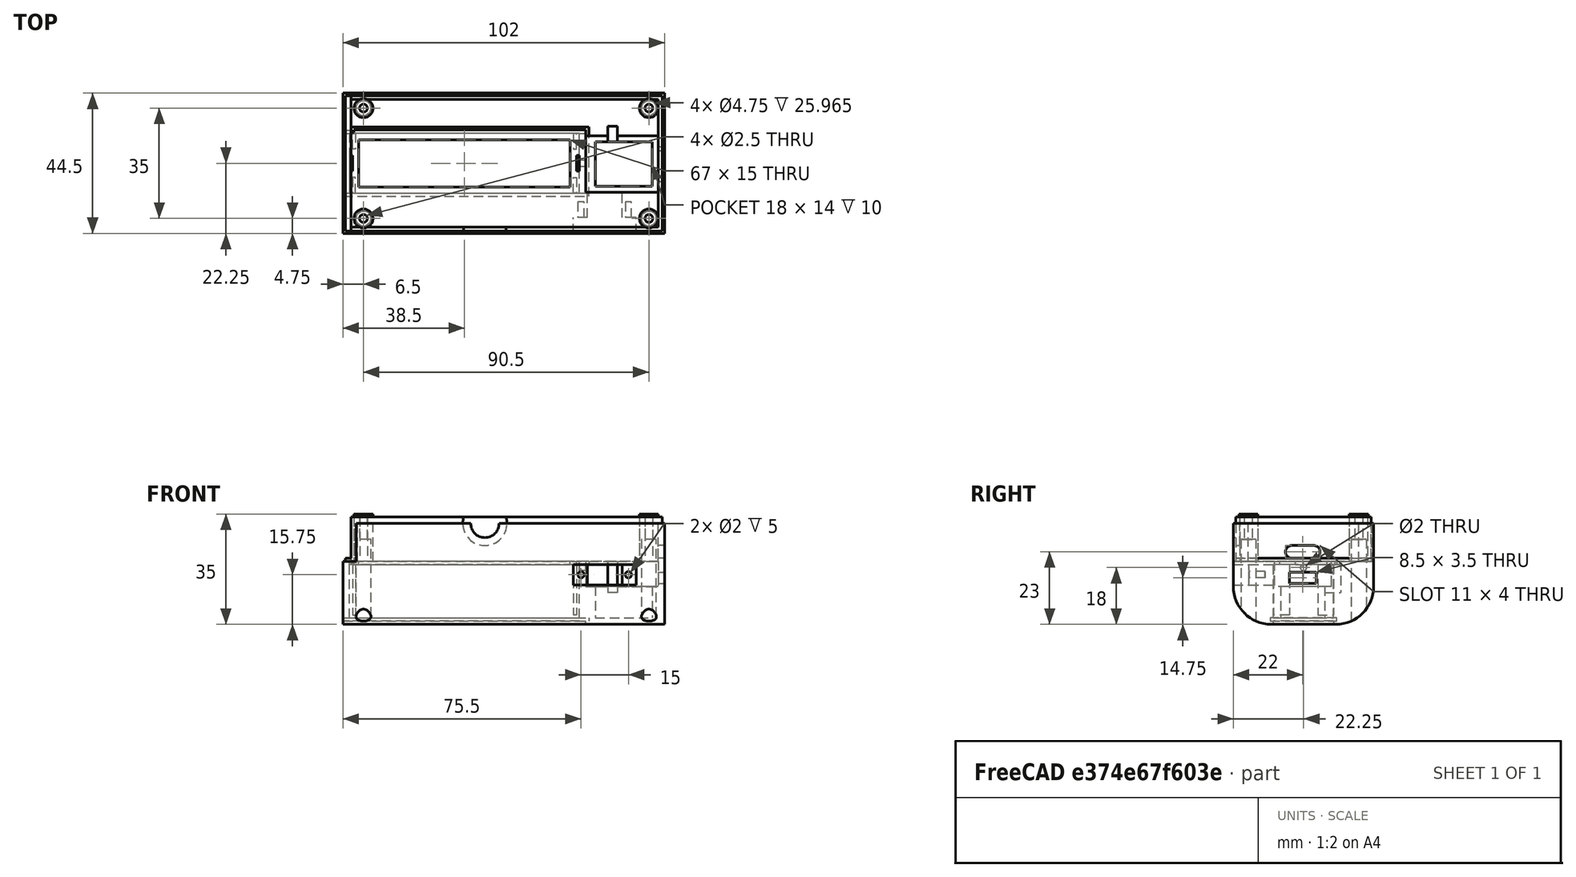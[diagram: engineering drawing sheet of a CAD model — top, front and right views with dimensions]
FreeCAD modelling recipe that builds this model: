
FCSTD DOCUMENT  (FreeCAD 0.20R)
Label: upper
License: All rights reserved
LicenseURL: http://en.wikipedia.org/wiki/All_rights_reserved
objects: Sketcher::SketchObject×27, PartDesign::Pocket×23, PartDesign::Pad×4, PartDesign::Plane×1, PartDesign::Fillet×1, PartDesign::Body×1
note: 85 computed .brp shape members not serialized (recipe doc carries the construction recipe); baked Part::Feature solids carry a one-line shape summary decoded from their .brp

FEATURE [Sketcher::SketchObject] Sketch  label="sketch_lower_base"
  FullyConstrained = true
  MapMode = 5
  Support = -> [XY_Plane]
  sketch-geometry (4):
    g0: LineSegment StartX=0 StartY=0 StartZ=0 EndX=102 EndY=0 EndZ=0
    g1: LineSegment StartX=102 StartY=0 StartZ=0 EndX=102 EndY=44.5 EndZ=0
    g2: LineSegment StartX=102 StartY=44.5 StartZ=0 EndX=0 EndY=44.5 EndZ=0
    g3: LineSegment StartX=0 StartY=44.5 StartZ=0 EndX=0 EndY=0 EndZ=0
  constraints (11):
    c: Coincident(g0,g1)
    c: Coincident(g1,g2)
    c: Coincident(g2,g3)
    c: Coincident(g3,g0)
    c: Horizontal(g0)
    c: Horizontal(g2)
    c: Vertical(g1)
    c: Vertical(g3)
    c: Coincident(g0,g-1)
    c: Distance(g2) = 102
    c: Distance(g3) = 44.5
FEATURE [PartDesign::Pad] Pad  label="pad_lower_base"
  Direction = (0,0,1)
  Length = 16
  Length2 = 10
  Profile = -> Sketch
  ReferenceAxis = -> Sketch [N_Axis]
  Type = 0
FEATURE [Sketcher::SketchObject] Sketch001  label="sketch_lower_base_hole"
  FullyConstrained = true
  MapMode = 5
  Placement = pos=(0,0,16) rot=(0,0,1;0rad)
  Support = -> [Pad]
  sketch-geometry (4):
    g0: LineSegment StartX=2.5 StartY=42.5 StartZ=0 EndX=100 EndY=42.5 EndZ=0
    g1: LineSegment StartX=100 StartY=42.5 StartZ=0 EndX=100 EndY=2 EndZ=0
    g2: LineSegment StartX=100 StartY=2 StartZ=0 EndX=2.5 EndY=2 EndZ=0
    g3: LineSegment StartX=2.5 StartY=2 StartZ=0 EndX=2.5 EndY=42.5 EndZ=0
  constraints (12):
    c: Coincident(g0,g1)
    c: Coincident(g1,g2)
    c: Coincident(g2,g3)
    c: Coincident(g3,g0)
    c: Horizontal(g0)
    c: Horizontal(g2)
    c: Vertical(g1)
    c: Vertical(g3)
    c: DistanceX(g-2,g2) = 2.5
    c: DistanceY(g-1,g2) = 2
    c: Distance(g0) = 97.5
    c: Distance(g1) = 40.5
FEATURE [PartDesign::Pocket] Pocket  label="pocket_lower_base_hole"
  BaseFeature = -> Pad
  Direction = (0,0,-1)
  Length = 14
  Length2 = 5
  Profile = -> Sketch001
  ReferenceAxis = -> Sketch001 [N_Axis]
  Type = 0
FEATURE [Sketcher::SketchObject] Sketch002  label="sketch_board_stands"
  FullyConstrained = true
  MapMode = 5
  Placement = pos=(0,0,2) rot=(0,0,1;0rad)
  Support = -> [Pocket]
  sketch-geometry (4):
    g0: Circle CenterX=6.5 CenterY=39.75 CenterZ=0 NormalX=0 NormalY=0 NormalZ=1 AngleXU=0 Radius=3
    g1: Circle CenterX=97 CenterY=39.75 CenterZ=0 NormalX=0 NormalY=0 NormalZ=1 AngleXU=0 Radius=3
    g2: Circle CenterX=6.5 CenterY=4.75 CenterZ=0 NormalX=0 NormalY=0 NormalZ=1 AngleXU=0 Radius=3
    g3: Circle CenterX=97 CenterY=4.75 CenterZ=0 NormalX=0 NormalY=0 NormalZ=1 AngleXU=0 Radius=3
  constraints (12):
    c: Equal(g0,g1)
    c: Equal(g1,g3)
    c: Equal(g3,g2)
    c: Distance(g0,g1) = 90.5
    c: Distance(g2,g3) = 90.5
    c: Diameter(g1) = 6
    c: Distance(g1,g3) = 35
    c: Distance(g0,g2) = 35
    c: DistanceX(g-2,g1) = 97
    c: DistanceX(g-2,g3) = 97
    c: DistanceY(g-1,g2) = 4.75
    c: DistanceY(g-1,g3) = 4.75
FEATURE [PartDesign::Pad] Pad001  label="pad_board_stands"
  BaseFeature = -> Pocket
  Direction = (0,0,1)
  Length = 15
  Length2 = 10
  Profile = -> Sketch002
  ReferenceAxis = -> Sketch002 [N_Axis]
  Type = 0
FEATURE [Sketcher::SketchObject] Sketch004  label="sketch_upper_base"
  FullyConstrained = true
  MapMode = 5
  Placement = pos=(0,0,0) rot=(1,0,0;3.14159rad)
  Support = -> [Pad001]
  sketch-geometry (4):
    g0: LineSegment StartX=0 StartY=0 StartZ=0 EndX=102 EndY=0 EndZ=0
    g1: LineSegment StartX=102 StartY=0 StartZ=0 EndX=102 EndY=-44.5 EndZ=0
    g2: LineSegment StartX=102 StartY=-44.5 StartZ=0 EndX=0 EndY=-44.5 EndZ=0
    g3: LineSegment StartX=0 StartY=-44.5 StartZ=0 EndX=0 EndY=0 EndZ=0
  constraints (12):
    c: Coincident(g0,g1)
    c: Coincident(g1,g2)
    c: Coincident(g2,g3)
    c: Coincident(g3,g0)
    c: Horizontal(g0)
    c: Horizontal(g2)
    c: Vertical(g1)
    c: Vertical(g3)
    c: PointOnObject(g0,g-2)
    c: Distance(g0) = 102
    c: Distance(g1) = 44.5
    c: DistanceY(g-1,g0) = 0
FEATURE [PartDesign::Pad] Pad002  label="pad_upper_base"
  BaseFeature = -> Pad001
  Direction = (0,0,-1)
  Length = 18
  Length2 = 10
  Profile = -> Sketch004
  ReferenceAxis = -> Sketch004 [N_Axis]
  Type = 0
FEATURE [Sketcher::SketchObject] Sketch003  label="sketch_battery_hole"
  FullyConstrained = true
  MapMode = 5
  Placement = pos=(0,0,-18) rot=(1,0,0;3.14159rad)
  Support = -> [Pad002]
  expr: Constraints[10] = -12.75
  sketch-geometry (4):
    g0: LineSegment StartX=2 StartY=-12.75 StartZ=0 EndX=75 EndY=-12.75 EndZ=0
    g1: LineSegment StartX=75 StartY=-12.75 StartZ=0 EndX=75 EndY=-31.75 EndZ=0
    g2: LineSegment StartX=75 StartY=-31.75 StartZ=0 EndX=2 EndY=-31.75 EndZ=0
    g3: LineSegment StartX=2 StartY=-31.75 StartZ=0 EndX=2 EndY=-12.75 EndZ=0
  constraints (12):
    c: Coincident(g0,g1)
    c: Coincident(g1,g2)
    c: Coincident(g2,g3)
    c: Coincident(g3,g0)
    c: Horizontal(g0)
    c: Horizontal(g2)
    c: Vertical(g1)
    c: Vertical(g3)
    c: Distance(g0) = 73
    c: Distance(g1) = 19
    c: DistanceY(g-1,g0) = -12.75
    c: DistanceX(g-2,g0) = 2
FEATURE [PartDesign::Pocket] Pocket001  label="pocket_battery_hole"
  BaseFeature = -> Pad002
  Direction = (0,0,1)
  Length = 19
  Length2 = 5
  Profile = -> Sketch003
  ReferenceAxis = -> Sketch003 [N_Axis]
  Type = 0
FEATURE [Sketcher::SketchObject] Sketch005  label="sketch_battery_thru_hole"
  FullyConstrained = true
  MapMode = 5
  Placement = pos=(0,0,1) rot=(1,0,0;3.14159rad)
  Support = -> [Pocket001]
  expr: Constraints[11] = -14.75
  sketch-geometry (4):
    g0: LineSegment StartX=5 StartY=-14.75 StartZ=0 EndX=72 EndY=-14.75 EndZ=0
    g1: LineSegment StartX=72 StartY=-14.75 StartZ=0 EndX=72 EndY=-29.75 EndZ=0
    g2: LineSegment StartX=72 StartY=-29.75 StartZ=0 EndX=5 EndY=-29.75 EndZ=0
    g3: LineSegment StartX=5 StartY=-29.75 StartZ=0 EndX=5 EndY=-14.75 EndZ=0
  constraints (12):
    c: Coincident(g0,g1)
    c: Coincident(g1,g2)
    c: Coincident(g2,g3)
    c: Coincident(g3,g0)
    c: Horizontal(g0)
    c: Horizontal(g2)
    c: Vertical(g1)
    c: Vertical(g3)
    c: Distance(g0) = 67
    c: Distance(g3) = 15
    c: DistanceX(g-2,g0) = 5
    c: DistanceY(g-1,g0) = -14.75
FEATURE [PartDesign::Pocket] Pocket002  label="pocket_battery_thru_hole"
  BaseFeature = -> Pocket001
  Direction = (0,0,1)
  Length = 5
  Length2 = 5
  Profile = -> Sketch005
  ReferenceAxis = -> Sketch005 [N_Axis]
  Type = 0
FEATURE [Sketcher::SketchObject] Sketch006  label="sketch_charge_module_hole"
  FullyConstrained = true
  MapMode = 5
  Placement = pos=(0,0,2) rot=(0,0,1;0rad)
  Support = -> [Pocket002]
  sketch-geometry (4):
    g0: LineSegment StartX=77 StartY=31 StartZ=0 EndX=100 EndY=31 EndZ=0
    g1: LineSegment StartX=100 StartY=31 StartZ=0 EndX=100 EndY=13 EndZ=0
    g2: LineSegment StartX=100 StartY=13 StartZ=0 EndX=77 EndY=13 EndZ=0
    g3: LineSegment StartX=77 StartY=13 StartZ=0 EndX=77 EndY=31 EndZ=0
  constraints (12):
    c: Coincident(g0,g1)
    c: Coincident(g1,g2)
    c: Coincident(g2,g3)
    c: Coincident(g3,g0)
    c: Horizontal(g0)
    c: Horizontal(g2)
    c: Vertical(g1)
    c: Vertical(g3)
    c: Distance(g1) = 18
    c: Distance(g0) = 23
    c: DistanceX(g-2,g0) = 77
    c: DistanceY(g-1,g2) = 13
FEATURE [PartDesign::Pocket] Pocket003  label="pocket_charge_module_hole"
  BaseFeature = -> Pocket002
  Direction = (0,0,-1)
  Length = 8
  Length2 = 5
  Profile = -> Sketch006
  ReferenceAxis = -> Sketch006 [N_Axis]
  Type = 0
FEATURE [Sketcher::SketchObject] Sketch009  label="sketch_charge_module_lower_hole"
  FullyConstrained = true
  MapMode = 5
  Placement = pos=(0,0,-6) rot=(0,0,1;0rad)
  Support = -> [Pocket003]
  sketch-geometry (4):
    g0: LineSegment StartX=80 StartY=29 StartZ=0 EndX=98 EndY=29 EndZ=0
    g1: LineSegment StartX=98 StartY=29 StartZ=0 EndX=98 EndY=15 EndZ=0
    g2: LineSegment StartX=98 StartY=15 StartZ=0 EndX=80 EndY=15 EndZ=0
    g3: LineSegment StartX=80 StartY=15 StartZ=0 EndX=80 EndY=29 EndZ=0
  constraints (12):
    c: Coincident(g0,g1)
    c: Coincident(g1,g2)
    c: Coincident(g2,g3)
    c: Coincident(g3,g0)
    c: Horizontal(g0)
    c: Horizontal(g2)
    c: Vertical(g1)
    c: Vertical(g3)
    c: Distance(g0) = 18
    c: Distance(g1) = 14
    c: DistanceY(g-1,g2) = 15
    c: DistanceX(g-2,g0) = 80
FEATURE [PartDesign::Pocket] Pocket006  label="pocket_charge_module_lower_hole"
  BaseFeature = -> Pocket003
  Direction = (0,0,-1)
  Length = 10
  Length2 = 5
  Profile = -> Sketch009
  ReferenceAxis = -> Sketch009 [N_Axis]
  Type = 0
FEATURE [PartDesign::Plane] DatumPlane  label="plane_upper"
  Length = 145.79
  MapMode = 5
  Placement = pos=(0,0,-18) rot=(1,0,0;3.14159rad)
  ResizeMode = 0
  Support = -> [Pocket006]
  Width = 88.2899
FEATURE [Sketcher::SketchObject] Sketch007  label="sketch_screw_holes"
  FullyConstrained = true
  MapMode = 5
  Placement = pos=(0,0,-18) rot=(1,0,0;3.14159rad)
  Support = -> [DatumPlane]
  sketch-geometry (4):
    g0: Circle CenterX=6.5 CenterY=-4.75 CenterZ=0 NormalX=0 NormalY=0 NormalZ=1 AngleXU=0 Radius=1.25
    g1: Circle CenterX=97 CenterY=-4.75 CenterZ=0 NormalX=0 NormalY=0 NormalZ=1 AngleXU=0 Radius=1.25
    g2: Circle CenterX=6.5 CenterY=-39.75 CenterZ=0 NormalX=0 NormalY=0 NormalZ=1 AngleXU=0 Radius=1.25
    g3: Circle CenterX=97 CenterY=-39.75 CenterZ=0 NormalX=0 NormalY=0 NormalZ=1 AngleXU=0 Radius=1.25
  constraints (12):
    c: Equal(g0,g2)
    c: Equal(g2,g3)
    c: Equal(g3,g1)
    c: Diameter(g0) = 2.5
    c: Distance(g3,g1) = 35
    c: Distance(g0,g2) = 35
    c: Distance(g0,g1) = 90.5
    c: Distance(g2,g3) = 90.5
    c: DistanceY(g-1,g0) = -4.75
    c: DistanceY(g-1,g1) = -4.75
    c: DistanceX(g-2,g1) = 97
    c: DistanceX(g-2,g3) = 97
FEATURE [Sketcher::SketchObject] Sketch008  label="sketch_screwdriver_hole"
  FullyConstrained = true
  MapMode = 5
  Placement = pos=(0,0,-18) rot=(1,0,0;3.14159rad)
  Support = -> [DatumPlane]
  sketch-geometry (4):
    g0: Circle CenterX=6.5 CenterY=-4.75 CenterZ=0 NormalX=0 NormalY=0 NormalZ=1 AngleXU=0 Radius=2.375
    g1: Circle CenterX=97 CenterY=-4.75 CenterZ=0 NormalX=0 NormalY=0 NormalZ=1 AngleXU=0 Radius=2.375
    g2: Circle CenterX=6.5 CenterY=-39.75 CenterZ=0 NormalX=0 NormalY=0 NormalZ=1 AngleXU=0 Radius=2.375
    g3: Circle CenterX=97 CenterY=-39.75 CenterZ=0 NormalX=0 NormalY=0 NormalZ=1 AngleXU=0 Radius=2.375
  constraints (12):
    c: Diameter(g0) = 4.75
    c: Equal(g0,g1)
    c: Equal(g1,g2)
    c: Equal(g2,g3)
    c: DistanceY(g-1,g0) = -4.75
    c: DistanceY(g-1,g1) = -4.75
    c: Distance(g3,g2) = 90.5
    c: Distance(g0,g1) = 90.5
    c: Distance(g1,g3) = 35
    c: Distance(g2,g0) = 35
    c: DistanceX(g-2,g3) = 97
    c: DistanceX(g-2,g1) = 97
FEATURE [PartDesign::Fillet] Fillet  label="fillet_upper_rounding"
  Base = -> Pocket006 [Edge13,Edge34]
  BaseFeature = -> Pocket006
  Radius = 12
  SupportTransform = false
  UseAllEdges = false
FEATURE [PartDesign::Pocket] Pocket004  label="pocket_screw_holes"
  BaseFeature = -> Fillet
  Direction = (0,0,1)
  Length = 35
  Length2 = 5
  Profile = -> Sketch007
  ReferenceAxis = -> Sketch007 [N_Axis]
  Type = 0
FEATURE [PartDesign::Pocket] Pocket005  label="pocket_screwdriver_hole"
  BaseFeature = -> Pocket004
  Direction = (0,0,1)
  Length = 27
  Length2 = 5
  Profile = -> Sketch008
  ReferenceAxis = -> Sketch008 [N_Axis]
  Type = 0
FEATURE [Sketcher::SketchObject] Sketch010  label="sketch_charge_module_usb_hole"
  FullyConstrained = true
  MapMode = 5
  Placement = pos=(100,0,0) rot=(0.57735,-0.57735,-0.57735;2.0944rad)
  Support = -> [Pocket005]
  sketch-geometry (4):
    g0: LineSegment StartX=-26.25 StartY=-1.5 StartZ=0 EndX=-17.75 EndY=-1.5 EndZ=0
    g1: LineSegment StartX=-17.75 StartY=-1.5 StartZ=0 EndX=-17.75 EndY=-5 EndZ=0
    g2: LineSegment StartX=-17.75 StartY=-5 StartZ=0 EndX=-26.25 EndY=-5 EndZ=0
    g3: LineSegment StartX=-26.25 StartY=-5 StartZ=0 EndX=-26.25 EndY=-1.5 EndZ=0
  constraints (12):
    c: Coincident(g0,g1)
    c: Coincident(g1,g2)
    c: Coincident(g2,g3)
    c: Coincident(g3,g0)
    c: Horizontal(g0)
    c: Horizontal(g2)
    c: Vertical(g1)
    c: Vertical(g3)
    c: Distance(g0) = 8.5
    c: Distance(g1) = 3.5
    c: DistanceY(g-1,g0) = -1.5
    c: DistanceX(g-2,g0) = -17.75
FEATURE [PartDesign::Pocket] Pocket007  label="pocket_charge_module_usb_hole"
  BaseFeature = -> Pocket005
  Direction = (1,0,0)
  Length = 5
  Length2 = 5
  Profile = -> Sketch010
  ReferenceAxis = -> Sketch010 [N_Axis]
  Type = 0
FEATURE [Sketcher::SketchObject] Sketch011  label="sketch_esp_usb_hole"
  FullyConstrained = true
  MapMode = 5
  Placement = pos=(102,0,0) rot=(0.57735,0.57735,0.57735;2.0944rad)
  Support = -> [Pocket007]
  sketch-geometry (4):
    g0: ArcOfCircle CenterX=18.5 CenterY=5 CenterZ=0 NormalX=0 NormalY=0 NormalZ=1 AngleXU=0 Radius=2 StartAngle=1.5708 EndAngle=4.71239
    g1: ArcOfCircle CenterX=25.5 CenterY=5 CenterZ=0 NormalX=0 NormalY=0 NormalZ=1 AngleXU=0 Radius=2 StartAngle=4.71239 EndAngle=7.85398
    g2: LineSegment StartX=18.5 StartY=3 StartZ=0 EndX=25.5 EndY=3 EndZ=0
    g3: LineSegment StartX=25.5 StartY=7 StartZ=0 EndX=18.5 EndY=7 EndZ=0
  constraints (10):
    c: Tangent(g0,g2) = -1.5708
    c: Tangent(g2,g1) = -1.5708
    c: Tangent(g1,g3) = -1.5708
    c: Tangent(g3,g0) = -1.5708
    c: Equal(g0,g1)
    c: Horizontal(g2)
    c: Radius(g1) = 2
    c: Distance(g0,g1) = 7
    c: DistanceY(g-1,g0) = 3
    c: DistanceX(g-2,g0) = 18.5
FEATURE [PartDesign::Pocket] Pocket008  label="pocket_esp_usb_hole"
  BaseFeature = -> Pocket007
  Direction = (-1,0,0)
  Length = 5
  Length2 = 5
  Profile = -> Sketch011
  ReferenceAxis = -> Sketch011 [N_Axis]
  Type = 0
FEATURE [Sketcher::SketchObject] Sketch012  label="sketch_ptt_hole"
  FullyConstrained = true
  MapMode = 5
  Placement = pos=(0,0,0) rot=(1,0,0;1.5708rad)
  Support = -> [Pocket008]
  sketch-geometry (1):
    g0: Circle CenterX=45 CenterY=14 CenterZ=0 NormalX=0 NormalY=0 NormalZ=1 AngleXU=0 Radius=4.5
  constraints (3):
    c: DistanceY(g-1,g0) = 14
    c: Diameter(g0) = 9
    c: DistanceX(g-2,g0) = 45
FEATURE [PartDesign::Pocket] Pocket009  label="pocket_ptt_hole"
  BaseFeature = -> Pocket008
  Direction = (0,1,-2e-16)
  Length = 10
  Length2 = 5
  Profile = -> Sketch012
  ReferenceAxis = -> Sketch012 [N_Axis]
  Type = 0
FEATURE [Sketcher::SketchObject] Sketch013  label="sketch_ptt_hole_rounding"
  FullyConstrained = true
  MapMode = 5
  Placement = pos=(0,2,0) rot=(0,0.707107,0.707107;3.14159rad)
  Support = -> [Pocket009]
  sketch-geometry (1):
    g0: Circle CenterX=-45 CenterY=14 CenterZ=0 NormalX=0 NormalY=0 NormalZ=1 AngleXU=0 Radius=7
  constraints (3):
    c: DistanceX(g-2,g0) = -45
    c: DistanceY(g-1,g0) = 14
    c: Diameter(g0) = 14
FEATURE [PartDesign::Pocket] Pocket010  label="pocket_ptt_hole_rounding"
  BaseFeature = -> Pocket009
  Direction = (0,-1,2e-16)
  Length = 1.2
  Length2 = 5
  Profile = -> Sketch013
  ReferenceAxis = -> Sketch013 [N_Axis]
  Type = 0
FEATURE [Sketcher::SketchObject] Sketch014  label="sketch_battery_lid_entrance"
  FullyConstrained = true
  MapMode = 5
  Placement = pos=(0,0,0) rot=(0.57735,-0.57735,-0.57735;2.0944rad)
  Support = -> [Pocket010]
  sketch-geometry (4):
    g0: LineSegment StartX=-31.75 StartY=-18 StartZ=0 EndX=-12.75 EndY=-18 EndZ=0
    g1: LineSegment StartX=-12.75 StartY=-18 StartZ=0 EndX=-12.75 EndY=-16 EndZ=0
    g2: LineSegment StartX=-12.75 StartY=-16 StartZ=0 EndX=-31.75 EndY=-16 EndZ=0
    g3: LineSegment StartX=-31.75 StartY=-16 StartZ=0 EndX=-31.75 EndY=-18 EndZ=0
  constraints (12):
    c: Coincident(g0,g1)
    c: Coincident(g1,g2)
    c: Coincident(g2,g3)
    c: Coincident(g3,g0)
    c: Horizontal(g0)
    c: Horizontal(g2)
    c: Vertical(g1)
    c: Vertical(g3)
    c: Distance(g1) = 2
    c: Distance(g2) = 19
    c: DistanceY(g-1,g1) = -16
    c: DistanceX(g-2,g0) = -12.75
FEATURE [PartDesign::Pocket] Pocket011  label="pocket_battery_lid_entrance"
  BaseFeature = -> Pocket010
  Direction = (1,0,0)
  Length = 77
  Length2 = 5
  Profile = -> Sketch014
  ReferenceAxis = -> Sketch014 [N_Axis]
  Type = 0
FEATURE [Sketcher::SketchObject] Sketch015  label="sketch_battery_lid_slider"
  FullyConstrained = true
  MapMode = 5
  Placement = pos=(0,0,0) rot=(0.57735,-0.57735,-0.57735;2.0944rad)
  Support = -> [Pocket011]
  sketch-geometry (4):
    g0: LineSegment StartX=-32.75 StartY=-16 StartZ=0 EndX=-11.75 EndY=-16 EndZ=0
    g1: LineSegment StartX=-11.75 StartY=-16 StartZ=0 EndX=-11.75 EndY=-17 EndZ=0
    g2: LineSegment StartX=-11.75 StartY=-17 StartZ=0 EndX=-32.75 EndY=-17 EndZ=0
    g3: LineSegment StartX=-32.75 StartY=-17 StartZ=0 EndX=-32.75 EndY=-16 EndZ=0
  constraints (12):
    c: Coincident(g0,g1)
    c: Coincident(g1,g2)
    c: Coincident(g2,g3)
    c: Coincident(g3,g0)
    c: Horizontal(g0)
    c: Horizontal(g2)
    c: Vertical(g1)
    c: Vertical(g3)
    c: Distance(g1) = 1
    c: DistanceY(g-1,g0) = -16
    c: Distance(g0) = 21
    c: DistanceX(g-2,g0) = -11.75
FEATURE [PartDesign::Pocket] Pocket012  label="pocket_battery_lid_slider"
  BaseFeature = -> Pocket011
  Direction = (1,0,0)
  Length = 78
  Length2 = 5
  Profile = -> Sketch015
  ReferenceAxis = -> Sketch015 [N_Axis]
  Type = 0
FEATURE [Sketcher::SketchObject] Sketch016  label="sketch_battery_contacts_holder"
  FullyConstrained = true
  MapMode = 5
  Placement = pos=(0,0,1) rot=(1,0,0;3.14159rad)
  Support = -> [Pocket012]
  sketch-geometry (16):
    g0: LineSegment StartX=3 StartY=-12.75 StartZ=0 EndX=4 EndY=-12.75 EndZ=0
    g1: LineSegment StartX=4 StartY=-12.75 StartZ=0 EndX=4 EndY=-17.75 EndZ=0
    g2: LineSegment StartX=4 StartY=-17.75 StartZ=0 EndX=3 EndY=-17.75 EndZ=0
    g3: LineSegment StartX=3 StartY=-17.75 StartZ=0 EndX=3 EndY=-12.75 EndZ=0
    g4: LineSegment StartX=4 StartY=-26.75 StartZ=0 EndX=3 EndY=-26.75 EndZ=0
    g5: LineSegment StartX=3 StartY=-26.75 StartZ=0 EndX=3 EndY=-31.75 EndZ=0
    g6: LineSegment StartX=3 StartY=-31.75 StartZ=0 EndX=4 EndY=-31.75 EndZ=0
    g7: LineSegment StartX=4 StartY=-31.75 StartZ=0 EndX=4 EndY=-26.75 EndZ=0
    g8: LineSegment StartX=73 StartY=-17.75 StartZ=0 EndX=74 EndY=-17.75 EndZ=0
    g9: LineSegment StartX=74 StartY=-17.75 StartZ=0 EndX=74 EndY=-12.75 EndZ=0
    g10: LineSegment StartX=74 StartY=-12.75 StartZ=0 EndX=73 EndY=-12.75 EndZ=0
    g11: LineSegment StartX=73 StartY=-12.75 StartZ=0 EndX=73 EndY=-17.75 EndZ=0
    g12: LineSegment StartX=73 StartY=-26.75 StartZ=0 EndX=74 EndY=-26.75 EndZ=0
    g13: LineSegment StartX=74 StartY=-26.75 StartZ=0 EndX=74 EndY=-31.75 EndZ=0
    g14: LineSegment StartX=74 StartY=-31.75 StartZ=0 EndX=73 EndY=-31.75 EndZ=0
    g15: LineSegment StartX=73 StartY=-31.75 StartZ=0 EndX=73 EndY=-26.75 EndZ=0
  constraints (48):
    c: Coincident(g0,g1)
    c: Coincident(g1,g2)
    c: Coincident(g2,g3)
    c: Coincident(g3,g0)
    c: Horizontal(g0)
    c: Horizontal(g2)
    c: Vertical(g1)
    c: Vertical(g3)
    c: Coincident(g4,g5)
    c: Coincident(g5,g6)
    c: Coincident(g6,g7)
    c: Coincident(g7,g4)
    c: Horizontal(g4)
    c: Horizontal(g6)
    c: Vertical(g5)
    c: Vertical(g7)
    c: Coincident(g8,g9)
    c: Coincident(g9,g10)
    c: Coincident(g10,g11)
    c: Coincident(g11,g8)
    c: Horizontal(g8)
    c: Horizontal(g10)
    c: Vertical(g9)
    c: Vertical(g11)
    c: Coincident(g12,g13)
    c: Coincident(g13,g14)
    c: Coincident(g14,g15)
    c: Coincident(g15,g12)
    c: Horizontal(g12)
    c: Horizontal(g14)
    c: Vertical(g13)
    c: Vertical(g15)
    c: Distance(g0) = 1
    c: Distance(g1) = 5
    c: Equal(g0,g4)
    c: Equal(g4,g12)
    c: Equal(g12,g10)
    c: Equal(g1,g7)
    c: Equal(g7,g13)
    c: Equal(g13,g9)
    c: DistanceX(g-2,g0) = 3
    c: DistanceX(g-2,g4) = 3
    c: DistanceY(g-1,g0) = -12.75
    c: DistanceY(g-1,g4) = -26.75
    c: DistanceY(g-1,g10) = -12.75
    c: DistanceY(g-1,g12) = -26.75
    c: DistanceX(g-2,g10) = 73
    c: DistanceX(g-2,g14) = 73
FEATURE [PartDesign::Pad] Pad003  label="pad_battery_contacts_holder"
  BaseFeature = -> Pocket012
  Direction = (0,0,-1)
  Length = 16
  Length2 = 10
  Profile = -> Sketch016
  ReferenceAxis = -> Sketch016 [N_Axis]
  Type = 0
FEATURE [Sketcher::SketchObject] Sketch017  label="sketch_minus_battery_hole"
  FullyConstrained = true
  MapMode = 5
  Placement = pos=(75,0,0) rot=(0.57735,-0.57735,-0.57735;2.0944rad)
  Support = -> [Pad003]
  sketch-geometry (1):
    g0: Circle CenterX=-22.25 CenterY=0 CenterZ=0 NormalX=0 NormalY=0 NormalZ=1 AngleXU=0 Radius=1
  constraints (3):
    c: Diameter(g0) = 2
    c: DistanceY(g-1,g0) = 0
    c: DistanceX(g-2,g0) = -22.25
FEATURE [PartDesign::Pocket] Pocket013  label="pocket_minus_battery_hole"
  BaseFeature = -> Pad003
  Direction = (1,0,0)
  Length = 5
  Length2 = 5
  Profile = -> Sketch017
  ReferenceAxis = -> Sketch017 [N_Axis]
  Type = 0
FEATURE [Sketcher::SketchObject] Sketch018  label="sketch_battery_contact_holes"
  FullyConstrained = true
  MapMode = 5
  Placement = pos=(0,0,1) rot=(1,0,0;3.14159rad)
  Support = -> [Pocket013]
  sketch-geometry (8):
    g0: LineSegment StartX=2 StartY=-19.75 StartZ=0 EndX=3 EndY=-19.75 EndZ=0
    g1: LineSegment StartX=3 StartY=-19.75 StartZ=0 EndX=3 EndY=-24.75 EndZ=0
    g2: LineSegment StartX=3 StartY=-24.75 StartZ=0 EndX=2 EndY=-24.75 EndZ=0
    g3: LineSegment StartX=2 StartY=-24.75 StartZ=0 EndX=2 EndY=-19.75 EndZ=0
    g4: LineSegment StartX=75 StartY=-19.75 StartZ=0 EndX=74 EndY=-19.75 EndZ=0
    g5: LineSegment StartX=74 StartY=-19.75 StartZ=0 EndX=74 EndY=-24.75 EndZ=0
    g6: LineSegment StartX=74 StartY=-24.75 StartZ=0 EndX=75 EndY=-24.75 EndZ=0
    g7: LineSegment StartX=75 StartY=-24.75 StartZ=0 EndX=75 EndY=-19.75 EndZ=0
  constraints (24):
    c: Coincident(g0,g1)
    c: Coincident(g1,g2)
    c: Coincident(g2,g3)
    c: Coincident(g3,g0)
    c: Horizontal(g0)
    c: Horizontal(g2)
    c: Vertical(g1)
    c: Vertical(g3)
    c: Coincident(g4,g5)
    c: Coincident(g5,g6)
    c: Coincident(g6,g7)
    c: Coincident(g7,g4)
    c: Horizontal(g4)
    c: Horizontal(g6)
    c: Vertical(g5)
    c: Vertical(g7)
    c: Distance(g0) = 1
    c: Distance(g1) = 5
    c: Equal(g0,g4)
    c: Equal(g1,g5)
    c: DistanceX(g-2,g0) = 2
    c: DistanceX(g-2,g4) = 74
    c: DistanceY(g-1,g4) = -19.75
    c: DistanceY(g-1,g0) = -19.75
FEATURE [PartDesign::Pocket] Pocket014  label="pocket_battery_contact_holes"
  BaseFeature = -> Pocket013
  Direction = (0,0,1)
  Length = 1
  Length2 = 5
  Profile = -> Sketch018
  ReferenceAxis = -> Sketch018 [N_Axis]
  Type = 0
FEATURE [Sketcher::SketchObject] Sketch019  label="sketch_power_switch_main_hole"
  FullyConstrained = true
  MapMode = 5
  Placement = pos=(0,0,0) rot=(1,0,0;1.5708rad)
  Support = -> [Pocket014]
  sketch-geometry (4):
    g0: LineSegment StartX=73 StartY=1 StartZ=0 EndX=93 EndY=1 EndZ=0
    g1: LineSegment StartX=93 StartY=1 StartZ=0 EndX=93 EndY=-5.5 EndZ=0
    g2: LineSegment StartX=93 StartY=-5.5 StartZ=0 EndX=73 EndY=-5.5 EndZ=0
    g3: LineSegment StartX=73 StartY=-5.5 StartZ=0 EndX=73 EndY=1 EndZ=0
  constraints (12):
    c: Coincident(g0,g1)
    c: Coincident(g1,g2)
    c: Coincident(g2,g3)
    c: Coincident(g3,g0)
    c: Horizontal(g0)
    c: Horizontal(g2)
    c: Vertical(g1)
    c: Vertical(g3)
    c: Distance(g0) = 20
    c: Distance(g1) = 6.5
    c: DistanceY(g-1,g0) = 1
    c: DistanceX(g-2,g2) = 73
FEATURE [PartDesign::Pocket] Pocket015  label="pocket_power_switch_main_hole"
  BaseFeature = -> Pocket014
  Direction = (0,1,-2e-16)
  Length = 5
  Length2 = 5
  Profile = -> Sketch019
  ReferenceAxis = -> Sketch019 [N_Axis]
  Type = 0
FEATURE [Sketcher::SketchObject] Sketch020  label="sketch_power_switch_inner_hole"
  FullyConstrained = true
  MapMode = 5
  Placement = pos=(0,5,-1.1e-15) rot=(1,0,0;1.5708rad)
  Support = -> [Pocket015]
  sketch-geometry (4):
    g0: LineSegment StartX=77.5 StartY=1 StartZ=0 EndX=88.5 EndY=1 EndZ=0
    g1: LineSegment StartX=88.5 StartY=1 StartZ=0 EndX=88.5 EndY=-5.5 EndZ=0
    g2: LineSegment StartX=88.5 StartY=-5.5 StartZ=0 EndX=77.5 EndY=-5.5 EndZ=0
    g3: LineSegment StartX=77.5 StartY=-5.5 StartZ=0 EndX=77.5 EndY=1 EndZ=0
  constraints (12):
    c: Coincident(g0,g1)
    c: Coincident(g1,g2)
    c: Coincident(g2,g3)
    c: Coincident(g3,g0)
    c: Horizontal(g0)
    c: Horizontal(g2)
    c: Vertical(g1)
    c: Vertical(g3)
    c: Distance(g3) = 6.5
    c: Distance(g2) = 11
    c: DistanceY(g-1,g0) = 1
    c: DistanceX(g-2,g0) = 77.5
FEATURE [PartDesign::Pocket] Pocket016  label="pocket_power_switch_inner_hole"
  BaseFeature = -> Pocket015
  Direction = (0,1,-2e-16)
  Length = 8
  Length2 = 5
  Profile = -> Sketch020
  ReferenceAxis = -> Sketch020 [N_Axis]
  Type = 0
FEATURE [Sketcher::SketchObject] Sketch021  label="sketch_power_switch_screw_holes"
  FullyConstrained = true
  MapMode = 5
  Placement = pos=(0,5,-1.1e-15) rot=(1,0,0;1.5708rad)
  Support = -> [Pocket016]
  sketch-geometry (2):
    g0: Circle CenterX=75.5 CenterY=-2.25 CenterZ=0 NormalX=0 NormalY=0 NormalZ=1 AngleXU=0 Radius=1
    g1: Circle CenterX=90.5 CenterY=-2.25 CenterZ=0 NormalX=0 NormalY=0 NormalZ=1 AngleXU=0 Radius=1
  constraints (6):
    c: Equal(g0,g1)
    c: Diameter(g0) = 2
    c: Distance(g0,g1) = 15
    c: DistanceY(g-1,g0) = -2.25
    c: DistanceY(g-1,g1) = -2.25
    c: DistanceX(g-2,g0) = 75.5
FEATURE [PartDesign::Pocket] Pocket017  label="pocket_power_switch_screw_holes"
  BaseFeature = -> Pocket016
  Direction = (0,1,-2e-16)
  Length = 5
  Length2 = 5
  Profile = -> Sketch021
  ReferenceAxis = -> Sketch021 [N_Axis]
  Type = 0
FEATURE [Sketcher::SketchObject] Sketch022  label="sketch_face_removal"
  FullyConstrained = true
  MapMode = 5
  Placement = pos=(0,0,16) rot=(0,0,1;0rad)
  Support = -> [Pocket017]
  sketch-geometry (4):
    g0: LineSegment StartX=0 StartY=44.5 StartZ=0 EndX=2.5 EndY=44.5 EndZ=0
    g1: LineSegment StartX=2.5 StartY=44.5 StartZ=0 EndX=2.5 EndY=0 EndZ=0
    g2: LineSegment StartX=2.5 StartY=0 StartZ=0 EndX=0 EndY=0 EndZ=0
    g3: LineSegment StartX=0 StartY=0 StartZ=0 EndX=0 EndY=44.5 EndZ=0
  constraints (12):
    c: Coincident(g0,g1)
    c: Coincident(g1,g2)
    c: Coincident(g2,g3)
    c: Coincident(g3,g0)
    c: Horizontal(g0)
    c: Horizontal(g2)
    c: Vertical(g1)
    c: Vertical(g3)
    c: PointOnObject(g0,g-2)
    c: PointOnObject(g1,g-1)
    c: Distance(g0) = 2.5
    c: Distance(g1) = 44.5
FEATURE [PartDesign::Pocket] Pocket018  label="pocket_face_removal"
  BaseFeature = -> Pocket017
  Direction = (0,0,-1)
  Length = 13
  Length2 = 5
  Profile = -> Sketch022
  ReferenceAxis = -> Sketch022 [N_Axis]
  Type = 0
FEATURE [Sketcher::SketchObject] Sketch023  label="sketch_outer_facet_removal"
  FullyConstrained = false
  MapMode = 5
  Placement = pos=(0,0,16) rot=(0,0,1;0rad)
  Support = -> [Pocket018]
  sketch-geometry (8):
    g0: LineSegment StartX=2.49905 StartY=44.5 StartZ=0 EndX=102 EndY=44.5 EndZ=0
    g1: LineSegment StartX=102 StartY=44.5 StartZ=0 EndX=102 EndY=0 EndZ=0
    g2: LineSegment StartX=102 StartY=0 StartZ=0 EndX=2.5 EndY=0 EndZ=0
    g3: LineSegment StartX=2.5 StartY=0 StartZ=0 EndX=2.5 EndY=0.8 EndZ=0
    g4: LineSegment StartX=2.5 StartY=0.8 StartZ=0 EndX=101.2 EndY=0.8 EndZ=0
    g5: LineSegment StartX=101.2 StartY=0.8 StartZ=0 EndX=101.2 EndY=43.7 EndZ=0
    g6: LineSegment StartX=101.2 StartY=43.7 StartZ=0 EndX=2.49905 EndY=43.7 EndZ=0
    g7: LineSegment StartX=2.49905 StartY=43.7 StartZ=0 EndX=2.49905 EndY=44.5 EndZ=0
  constraints (23):
    c: Horizontal(g0)
    c: Coincident(g1,g0)
    c: Vertical(g1)
    c: Coincident(g2,g1)
    c: PointOnObject(g2,g-1)
    c: Horizontal(g2)
    c: Coincident(g3,g2)
    c: Vertical(g3)
    c: Coincident(g4,g3)
    c: Horizontal(g4)
    c: Coincident(g5,g4)
    c: Vertical(g5)
    c: Coincident(g6,g5)
    c: Horizontal(g6)
    c: Coincident(g7,g6)
    c: Coincident(g7,g0)
    c: Vertical(g7)
    c: Distance(g7) = 0.8
    c: Equal(g7,g3)
    c: Distance(g5,g1) = 0.8
    c: DistanceX(g-2,g2) = 2.5
    c: DistanceY(g-1,g0) = 44.5
    c: DistanceX(g-2,g0) = 102
FEATURE [PartDesign::Pocket] Pocket019  label="pocket_outer_facet_removal"
  BaseFeature = -> Pocket018
  Direction = (0,0,-1)
  Length = 2
  Length2 = 5
  Profile = -> Sketch023
  ReferenceAxis = -> Sketch023 [N_Axis]
  Type = 0
FEATURE [Sketcher::SketchObject] Sketch024  label="sketch_outer_front_facet_removal"
  FullyConstrained = false
  MapMode = 5
  Placement = pos=(0,0,16) rot=(0,0,1;0rad)
  Support = -> [Pocket019]
  sketch-geometry (8):
    g0: LineSegment StartX=4.16371 StartY=0 StartZ=0 EndX=4.16371 EndY=0.8 EndZ=0
    g1: LineSegment StartX=4.16371 StartY=0.8 StartZ=0 EndX=0.800622 EndY=0.8 EndZ=0
    g2: LineSegment StartX=0.800622 StartY=0.8 StartZ=0 EndX=0.800622 EndY=43.7 EndZ=0
    g3: LineSegment StartX=0.800622 StartY=43.7 StartZ=0 EndX=4.5 EndY=43.7 EndZ=0
    g4: LineSegment StartX=4.5 StartY=43.7 StartZ=0 EndX=4.5 EndY=44.5 EndZ=0
    g5: LineSegment StartX=4.5 StartY=44.5 StartZ=0 EndX=0 EndY=44.5 EndZ=0
    g6: LineSegment StartX=0 StartY=44.5 StartZ=0 EndX=0 EndY=0 EndZ=0
    g7: LineSegment StartX=0 StartY=0 StartZ=0 EndX=4.16371 EndY=0 EndZ=0
  constraints (21):
    c: Coincident(g4,g5)
    c: Coincident(g4,g3)
    c: Coincident(g6,g5)
    c: Coincident(g2,g3)
    c: Coincident(g1,g2)
    c: Coincident(g1,g0)
    c: Coincident(g0,g7)
    c: Coincident(g7,g6)
    c: Distance(g4) = 0.8
    c: Distance(g0) = 0.8
    c: Parallel(g6,g2)
    c: Parallel(g2,g0)
    c: Parallel(g0,g4)
    c: Parallel(g4,g-2)
    c: Parallel(g5,g3)
    c: Parallel(g3,g1)
    c: Parallel(g1,g7)
    c: Parallel(g7,g-1)
    c: Distance(g5) = 4.5
    c: Coincident(g6,g-1)
    c: Distance(g6) = 44.5
FEATURE [PartDesign::Pocket] Pocket020  label="pocket_outer_front_facet_removal"
  BaseFeature = -> Pocket019
  Direction = (0,0,-1)
  Length = 14
  Length2 = 5
  Profile = -> Sketch024
  ReferenceAxis = -> Sketch024 [N_Axis]
  Type = 0
FEATURE [Sketcher::SketchObject] Sketch025  label="sketch_plus_wire_guide"
  FullyConstrained = false
  MapMode = 5
  Placement = pos=(0,0,2) rot=(0,0,1;0rad)
  Support = -> [Pocket020]
  sketch-geometry (8):
    g0: LineSegment StartX=3.5 StartY=32.1271 StartZ=0 EndX=3.5 EndY=32.8189 EndZ=0
    g1: LineSegment StartX=3.5 StartY=32.8189 StartZ=0 EndX=77 EndY=32.8189 EndZ=0
    g2: LineSegment StartX=77 StartY=32.8189 StartZ=0 EndX=77 EndY=31 EndZ=0
    g3: LineSegment StartX=77 StartY=31 StartZ=0 EndX=78 EndY=31 EndZ=0
    g4: LineSegment StartX=78 StartY=31 StartZ=0 EndX=78 EndY=33.8189 EndZ=0
    g5: LineSegment StartX=78 StartY=33.8189 StartZ=0 EndX=2.5 EndY=33.8189 EndZ=0
    g6: LineSegment StartX=2.5 StartY=33.8189 StartZ=0 EndX=2.5 EndY=32.1271 EndZ=0
    g7: LineSegment StartX=3.5 StartY=32.1271 StartZ=0 EndX=2.5 EndY=32.1271 EndZ=0
  constraints (22):
    c: Vertical(g0)
    c: Coincident(g1,g0)
    c: Horizontal(g1)
    c: Coincident(g2,g1)
    c: Vertical(g2)
    c: Coincident(g3,g2)
    c: Horizontal(g3)
    c: Coincident(g4,g3)
    c: Vertical(g4)
    c: Coincident(g5,g4)
    c: Horizontal(g5)
    c: Coincident(g6,g5)
    c: Vertical(g6)
    c: Coincident(g7,g0)
    c: Coincident(g7,g6)
    c: Horizontal(g7)
    c: Distance(g0,g6) = 1
    c: Distance(g0,g5) = 1
    c: Distance(g1,g4) = 1
    c: DistanceX(g-2,g6) = 2.5
    c: DistanceX(g-2,g2) = 77
    c: DistanceY(g-1,g3) = 31
FEATURE [PartDesign::Pocket] Pocket021  label="pocket_plus_wire_guide"
  BaseFeature = -> Pocket020
  Direction = (0,0,-1)
  Length = 1
  Length2 = 5
  Profile = -> Sketch025
  ReferenceAxis = -> Sketch025 [N_Axis]
  Type = 0
FEATURE [Sketcher::SketchObject] Sketch026  label="sketch_charger_to_esp_hole"
  FullyConstrained = true
  MapMode = 5
  Placement = pos=(0,0,2) rot=(0,0,1;0rad)
  Support = -> [Pocket021]
  sketch-geometry (4):
    g0: LineSegment StartX=84 StartY=34 StartZ=0 EndX=87 EndY=34 EndZ=0
    g1: LineSegment StartX=87 StartY=34 StartZ=0 EndX=87 EndY=29 EndZ=0
    g2: LineSegment StartX=87 StartY=29 StartZ=0 EndX=84 EndY=29 EndZ=0
    g3: LineSegment StartX=84 StartY=29 StartZ=0 EndX=84 EndY=34 EndZ=0
  constraints (12):
    c: Coincident(g0,g1)
    c: Coincident(g1,g2)
    c: Coincident(g2,g3)
    c: Coincident(g3,g0)
    c: Horizontal(g0)
    c: Horizontal(g2)
    c: Vertical(g1)
    c: Vertical(g3)
    c: Distance(g0) = 3
    c: Distance(g1) = 5
    c: DistanceY(g-1,g2) = 29
    c: DistanceX(g-2,g2) = 84
FEATURE [PartDesign::Pocket] Pocket022  label="pocket_charger_to_esp_hole"
  BaseFeature = -> Pocket021
  Direction = (0,0,-1)
  Length = 10
  Length2 = 5
  Profile = -> Sketch026
  ReferenceAxis = -> Sketch026 [N_Axis]
  Type = 0
FEATURE [PartDesign::Body] Body
  Group = -> [Sketch,Pad,Sketch001,Pocket,Sketch002,Pad001,Sketch004,Pad002,Sketch003,Pocket001,Sketch005,Pocket002,Sketch006,Pocket003,Pocket006,Fillet,DatumPlane,Sketch007,Pocket004,Sketch008,Pocket005,Sketch009,Sketch010,Pocket007,Sketch011,Pocket008,Sketch012,Pocket009,Sketch013,Pocket010,Sketch014,Pocket011,Sketch015,Pocket012,Sketch016,Pad003,Sketch017,Pocket013,Sketch018,Pocket014,Sketch019,Pocket015,+14 more]
  Origin = -> Origin
  Tip = -> Pocket022
